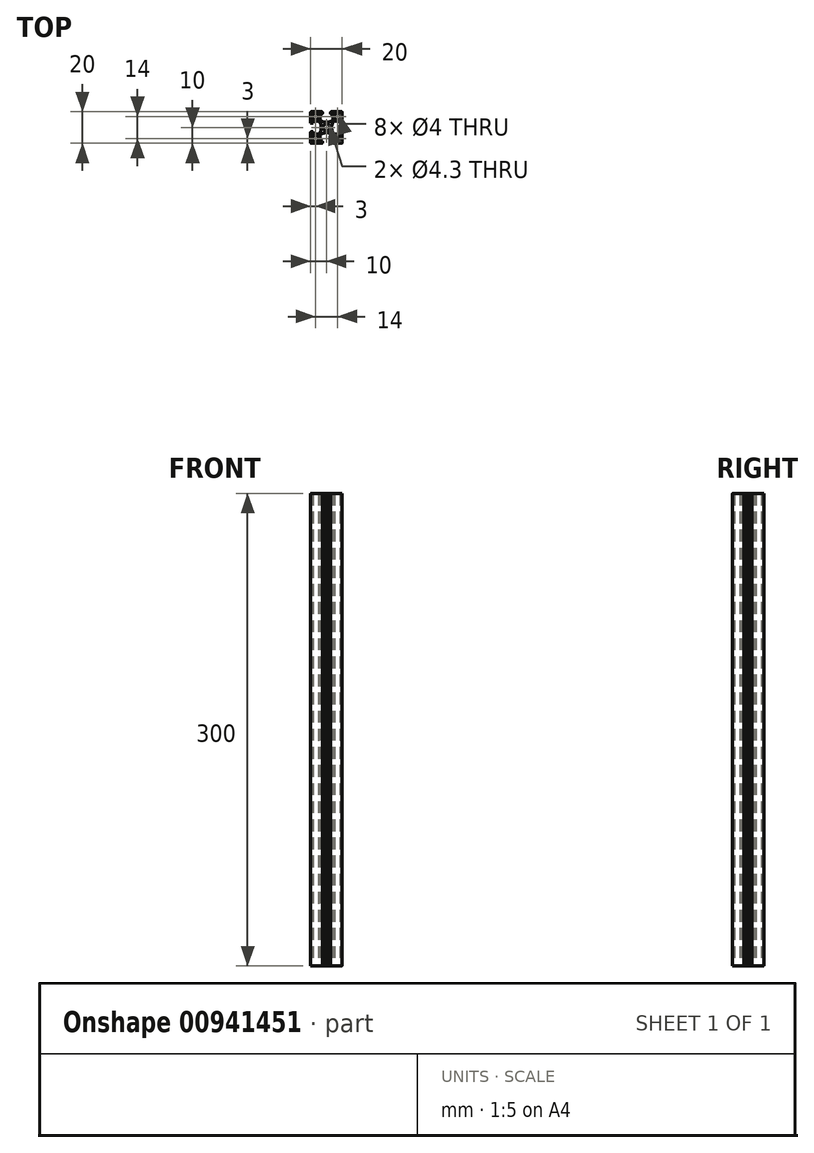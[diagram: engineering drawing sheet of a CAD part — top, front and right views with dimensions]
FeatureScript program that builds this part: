
annotation { "Feature Type Name" : "Feature", "Feature Type Description" : "" }
export const myFeature = defineFeature(function(context is Context, id is Id, definition is map)
    precondition{}
    {
        {
            var Q0;
            Q0=qCreatedBy(makeId("Top.planeOp"),FACE);
            var sketch = newSketch(context, id + "F0", { "sketchPlane" : qUnion([Q0])});
            skLineSegment(sketch, "E0", {"start": v(-11.2, 0) * mm, "end": v(11.2, 0) * mm});
            skCircle(sketch, "E1", {"center": v(0, 0) * mm, "radius": 2.15 * mm});
            skLineSegment(sketch, "E2", {"start": v(4.15, 4.94) * mm, "end": v(4.15, 8.2) * mm});
            skArc(sketch, "E3", {"start": v(4.15, 8.2) * mm, "mid": v(4.06, 8.41) * mm, "end": v(3.85, 8.5) * mm});
            skLineSegment(sketch, "E4", {"start": v(3.85, 8.5) * mm, "end": v(2.95, 8.5) * mm});
            skArc(sketch, "E5", {"start": v(2.95, 8.5) * mm, "mid": v(2.74, 8.59) * mm, "end": v(2.65, 8.8) * mm});
            skLineSegment(sketch, "E6", {"start": v(2.65, 8.8) * mm, "end": v(2.65, 9.7) * mm});
            skArc(sketch, "E7", {"start": v(2.65, 9.7) * mm, "mid": v(2.74, 9.91) * mm, "end": v(2.95, 10) * mm});
            skLineSegment(sketch, "E8", {"start": v(2.95, 10) * mm, "end": v(9.7, 10) * mm});
            skArc(sketch, "E9", {"start": v(9.7, 10) * mm, "mid": v(9.91, 9.91) * mm, "end": v(10, 9.7) * mm});
            skLineSegment(sketch, "E10", {"start": v(10, 9.7) * mm, "end": v(10, 2.95) * mm});
            skArc(sketch, "E11", {"start": v(10, 2.95) * mm, "mid": v(9.91, 2.74) * mm, "end": v(9.7, 2.65) * mm});
            skLineSegment(sketch, "E12", {"start": v(9.7, 2.65) * mm, "end": v(8.8, 2.65) * mm});
            skArc(sketch, "E13", {"start": v(8.8, 2.65) * mm, "mid": v(8.59, 2.74) * mm, "end": v(8.5, 2.95) * mm});
            skLineSegment(sketch, "E14", {"start": v(8.5, 2.95) * mm, "end": v(8.5, 3.85) * mm});
            skArc(sketch, "E15", {"start": v(8.5, 3.85) * mm, "mid": v(8.41, 4.06) * mm, "end": v(8.2, 4.15) * mm});
            skLineSegment(sketch, "E16", {"start": v(8.2, 4.15) * mm, "end": v(4.94, 4.15) * mm});
            skArc(sketch, "E17", {"start": v(4.94, 4.15) * mm, "mid": v(4.81, 4.12) * mm, "end": v(4.7, 4.04) * mm});
            skArc(sketch, "E18", {"start": v(4.7, 4.04) * mm, "mid": v(3.71, 2.28) * mm, "end": v(3.3, 0.3) * mm});
            skLineSegment(sketch, "E19", {"start": v(3.3, 0.3) * mm, "end": v(3, 0) * mm});
            skLineSegment(sketch, "E20", {"start": v(3, 0) * mm, "end": v(3.3, -0.3) * mm});
            skArc(sketch, "E21", {"start": v(3.3, -0.3) * mm, "mid": v(3.71, -2.28) * mm, "end": v(4.7, -4.04) * mm});
            skArc(sketch, "E22", {"start": v(4.7, -4.04) * mm, "mid": v(4.81, -4.12) * mm, "end": v(4.94, -4.15) * mm});
            skLineSegment(sketch, "E23", {"start": v(4.94, -4.15) * mm, "end": v(8.2, -4.15) * mm});
            skArc(sketch, "E24", {"start": v(8.2, -4.15) * mm, "mid": v(8.41, -4.06) * mm, "end": v(8.5, -3.85) * mm});
            skLineSegment(sketch, "E25", {"start": v(8.5, -3.85) * mm, "end": v(8.5, -2.95) * mm});
            skArc(sketch, "E26", {"start": v(8.5, -2.95) * mm, "mid": v(8.59, -2.74) * mm, "end": v(8.8, -2.65) * mm});
            skLineSegment(sketch, "E27", {"start": v(8.8, -2.65) * mm, "end": v(9.7, -2.65) * mm});
            skArc(sketch, "E28", {"start": v(9.7, -2.65) * mm, "mid": v(9.91, -2.74) * mm, "end": v(10, -2.95) * mm});
            skLineSegment(sketch, "E29", {"start": v(10, -2.95) * mm, "end": v(10, -9.7) * mm});
            skArc(sketch, "E30", {"start": v(10, -9.7) * mm, "mid": v(9.91, -9.91) * mm, "end": v(9.7, -10) * mm});
            skLineSegment(sketch, "E31", {"start": v(9.7, -10) * mm, "end": v(2.95, -10) * mm});
            skArc(sketch, "E32", {"start": v(2.95, -10) * mm, "mid": v(2.74, -9.91) * mm, "end": v(2.65, -9.7) * mm});
            skLineSegment(sketch, "E33", {"start": v(2.65, -9.7) * mm, "end": v(2.65, -8.8) * mm});
            skArc(sketch, "E34", {"start": v(2.65, -8.8) * mm, "mid": v(2.74, -8.59) * mm, "end": v(2.95, -8.5) * mm});
            skLineSegment(sketch, "E35", {"start": v(2.95, -8.5) * mm, "end": v(3.85, -8.5) * mm});
            skArc(sketch, "E36", {"start": v(3.85, -8.5) * mm, "mid": v(4.06, -8.41) * mm, "end": v(4.15, -8.2) * mm});
            skLineSegment(sketch, "E37", {"start": v(4.15, -8.2) * mm, "end": v(4.15, -4.94) * mm});
            skArc(sketch, "E38", {"start": v(4.15, -4.94) * mm, "mid": v(4.12, -4.81) * mm, "end": v(4.04, -4.7) * mm});
            skArc(sketch, "E39", {"start": v(4.04, -4.7) * mm, "mid": v(2.28, -3.71) * mm, "end": v(0.3, -3.3) * mm});
            skLineSegment(sketch, "E40", {"start": v(0.3, -3.3) * mm, "end": v(0, -3) * mm});
            skLineSegment(sketch, "E41", {"start": v(0, -3) * mm, "end": v(-0.3, -3.3) * mm});
            skArc(sketch, "E42", {"start": v(-0.3, -3.3) * mm, "mid": v(-2.28, -3.71) * mm, "end": v(-4.04, -4.7) * mm});
            skArc(sketch, "E43", {"start": v(-4.04, -4.7) * mm, "mid": v(-4.12, -4.81) * mm, "end": v(-4.15, -4.94) * mm});
            skLineSegment(sketch, "E44", {"start": v(-4.15, -4.94) * mm, "end": v(-4.15, -8.2) * mm});
            skArc(sketch, "E45", {"start": v(-4.15, -8.2) * mm, "mid": v(-4.06, -8.41) * mm, "end": v(-3.85, -8.5) * mm});
            skLineSegment(sketch, "E46", {"start": v(-3.85, -8.5) * mm, "end": v(-2.95, -8.5) * mm});
            skArc(sketch, "E47", {"start": v(-2.95, -8.5) * mm, "mid": v(-2.74, -8.59) * mm, "end": v(-2.65, -8.8) * mm});
            skLineSegment(sketch, "E48", {"start": v(-2.65, -8.8) * mm, "end": v(-2.65, -9.7) * mm});
            skArc(sketch, "E49", {"start": v(-2.65, -9.7) * mm, "mid": v(-2.74, -9.91) * mm, "end": v(-2.95, -10) * mm});
            skLineSegment(sketch, "E50", {"start": v(-2.95, -10) * mm, "end": v(-9.7, -10) * mm});
            skArc(sketch, "E51", {"start": v(-9.7, -10) * mm, "mid": v(-9.91, -9.91) * mm, "end": v(-10, -9.7) * mm});
            skLineSegment(sketch, "E52", {"start": v(-10, -9.7) * mm, "end": v(-10, -2.95) * mm});
            skArc(sketch, "E53", {"start": v(-10, -2.95) * mm, "mid": v(-9.91, -2.74) * mm, "end": v(-9.7, -2.65) * mm});
            skLineSegment(sketch, "E54", {"start": v(-9.7, -2.65) * mm, "end": v(-8.8, -2.65) * mm});
            skArc(sketch, "E55", {"start": v(-8.8, -2.65) * mm, "mid": v(-8.59, -2.74) * mm, "end": v(-8.5, -2.95) * mm});
            skLineSegment(sketch, "E56", {"start": v(-8.5, -2.95) * mm, "end": v(-8.5, -3.85) * mm});
            skArc(sketch, "E57", {"start": v(-8.5, -3.85) * mm, "mid": v(-8.41, -4.06) * mm, "end": v(-8.2, -4.15) * mm});
            skLineSegment(sketch, "E58", {"start": v(-8.2, -4.15) * mm, "end": v(-4.94, -4.15) * mm});
            skArc(sketch, "E59", {"start": v(-4.94, -4.15) * mm, "mid": v(-4.81, -4.12) * mm, "end": v(-4.7, -4.04) * mm});
            skArc(sketch, "E60", {"start": v(-4.7, -4.04) * mm, "mid": v(-3.71, -2.28) * mm, "end": v(-3.3, -0.3) * mm});
            skLineSegment(sketch, "E61", {"start": v(-3.3, -0.3) * mm, "end": v(-3, 0) * mm});
            skLineSegment(sketch, "E62", {"start": v(-3, 0) * mm, "end": v(-3.3, 0.3) * mm});
            skArc(sketch, "E63", {"start": v(-3.3, 0.3) * mm, "mid": v(-3.71, 2.28) * mm, "end": v(-4.7, 4.04) * mm});
            skArc(sketch, "E64", {"start": v(-4.7, 4.04) * mm, "mid": v(-4.81, 4.12) * mm, "end": v(-4.94, 4.15) * mm});
            skLineSegment(sketch, "E65", {"start": v(-4.94, 4.15) * mm, "end": v(-8.2, 4.15) * mm});
            skArc(sketch, "E66", {"start": v(-8.2, 4.15) * mm, "mid": v(-8.41, 4.06) * mm, "end": v(-8.5, 3.85) * mm});
            skLineSegment(sketch, "E67", {"start": v(-8.5, 3.85) * mm, "end": v(-8.5, 2.95) * mm});
            skArc(sketch, "E68", {"start": v(-8.5, 2.95) * mm, "mid": v(-8.59, 2.74) * mm, "end": v(-8.8, 2.65) * mm});
            skLineSegment(sketch, "E69", {"start": v(-8.8, 2.65) * mm, "end": v(-9.7, 2.65) * mm});
            skArc(sketch, "E70", {"start": v(-9.7, 2.65) * mm, "mid": v(-9.91, 2.74) * mm, "end": v(-10, 2.95) * mm});
            skLineSegment(sketch, "E71", {"start": v(-10, 2.95) * mm, "end": v(-10, 9.7) * mm});
            skArc(sketch, "E72", {"start": v(-10, 9.7) * mm, "mid": v(-9.91, 9.91) * mm, "end": v(-9.7, 10) * mm});
            skLineSegment(sketch, "E73", {"start": v(-9.7, 10) * mm, "end": v(-2.95, 10) * mm});
            skArc(sketch, "E74", {"start": v(-2.95, 10) * mm, "mid": v(-2.74, 9.91) * mm, "end": v(-2.65, 9.7) * mm});
            skLineSegment(sketch, "E75", {"start": v(-2.65, 9.7) * mm, "end": v(-2.65, 8.8) * mm});
            skArc(sketch, "E76", {"start": v(-2.65, 8.8) * mm, "mid": v(-2.74, 8.59) * mm, "end": v(-2.95, 8.5) * mm});
            skLineSegment(sketch, "E77", {"start": v(-2.95, 8.5) * mm, "end": v(-3.85, 8.5) * mm});
            skArc(sketch, "E78", {"start": v(-3.85, 8.5) * mm, "mid": v(-4.06, 8.41) * mm, "end": v(-4.15, 8.2) * mm});
            skLineSegment(sketch, "E79", {"start": v(-4.15, 8.2) * mm, "end": v(-4.15, 4.94) * mm});
            skArc(sketch, "E80", {"start": v(-4.15, 4.94) * mm, "mid": v(-4.12, 4.81) * mm, "end": v(-4.04, 4.7) * mm});
            skArc(sketch, "E81", {"start": v(-4.04, 4.7) * mm, "mid": v(-2.28, 3.71) * mm, "end": v(-0.3, 3.3) * mm});
            skLineSegment(sketch, "E82", {"start": v(-0.3, 3.3) * mm, "end": v(0, 3) * mm});
            skLineSegment(sketch, "E83", {"start": v(0, 3) * mm, "end": v(0.3, 3.3) * mm});
            skArc(sketch, "E84", {"start": v(0.3, 3.3) * mm, "mid": v(2.28, 3.71) * mm, "end": v(4.04, 4.7) * mm});
            skArc(sketch, "E85", {"start": v(4.04, 4.7) * mm, "mid": v(4.12, 4.81) * mm, "end": v(4.15, 4.94) * mm});
            skLineSegment(sketch, "E86", {"start": v(-9.5, 7) * mm, "end": v(-4.5, 7) * mm});
            skLineSegment(sketch, "E87", {"start": v(-7, 9.5) * mm, "end": v(-7, 4.5) * mm});
            skCircle(sketch, "E88", {"center": v(-7, 7) * mm, "radius": 2 * mm});
            skLineSegment(sketch, "E89", {"start": v(-9.5, -7) * mm, "end": v(-4.5, -7) * mm});
            skLineSegment(sketch, "E90", {"start": v(-7, -9.5) * mm, "end": v(-7, -4.5) * mm});
            skCircle(sketch, "E91", {"center": v(-7, -7) * mm, "radius": 2 * mm});
            skLineSegment(sketch, "E92", {"start": v(0, 11.2) * mm, "end": v(0, -11.2) * mm});
            skLineSegment(sketch, "E93", {"start": v(9.5, 7) * mm, "end": v(4.5, 7) * mm});
            skLineSegment(sketch, "E94", {"start": v(7, 9.5) * mm, "end": v(7, 4.5) * mm});
            skCircle(sketch, "E95", {"center": v(7, 7) * mm, "radius": 2 * mm});
            skCircle(sketch, "E96", {"center": v(7, -7) * mm, "radius": 2 * mm});
            skLineSegment(sketch, "E97", {"start": v(7, -9.5) * mm, "end": v(7, -4.5) * mm});
            skLineSegment(sketch, "E98", {"start": v(9.5, -7) * mm, "end": v(4.5, -7) * mm});
            skSolve(sketch);
        }
        {
            var Q0;
            {var subQ0=sQuery(id+"F0.wireOp",EDGE,"E62");Q0=makeQuery(id+"F0.imprint","IMPRINT",FACE,{"disambiguationData":[TD([[makeQuery(id+"F0.imprint","IMPRINT",EDGE,{"derivedFrom":subQ0}),-1.0]])]});}
            var Q1;
            Q1=makeQuery(id+"F0.imprint","IMPRINT",FACE,{"disambiguationData":[TD([[makeQuery(id+"F0.imprint","IMPRINT",EDGE,{"derivedFrom":sQuery(id+"F0.wireOp",EDGE,"E2")}),-1.0]])]});
            var Q2;
            {var subQ10=sQuery(id+"F0.wireOp",EDGE,"E20");Q2=makeQuery(id+"F0.imprint","IMPRINT",FACE,{"disambiguationData":[TD([[makeQuery(id+"F0.imprint","IMPRINT",EDGE,{"derivedFrom":subQ10}),-1.0]])]});}
            var Q3;
            {var subQ1=sQuery(id+"F0.wireOp",EDGE,"E41");Q3=makeQuery(id+"F0.imprint","IMPRINT",FACE,{"disambiguationData":[TD([[makeQuery(id+"F0.imprint","IMPRINT",EDGE,{"derivedFrom":subQ1}),-1.0]])]});}
            extrude(context, id + "F1", {"entities" : qUnion([Q0, Q1, Q2, Q3]), "depth" : 300 * mm, "offsetDistance" : 25 * mm});
        }
    });
